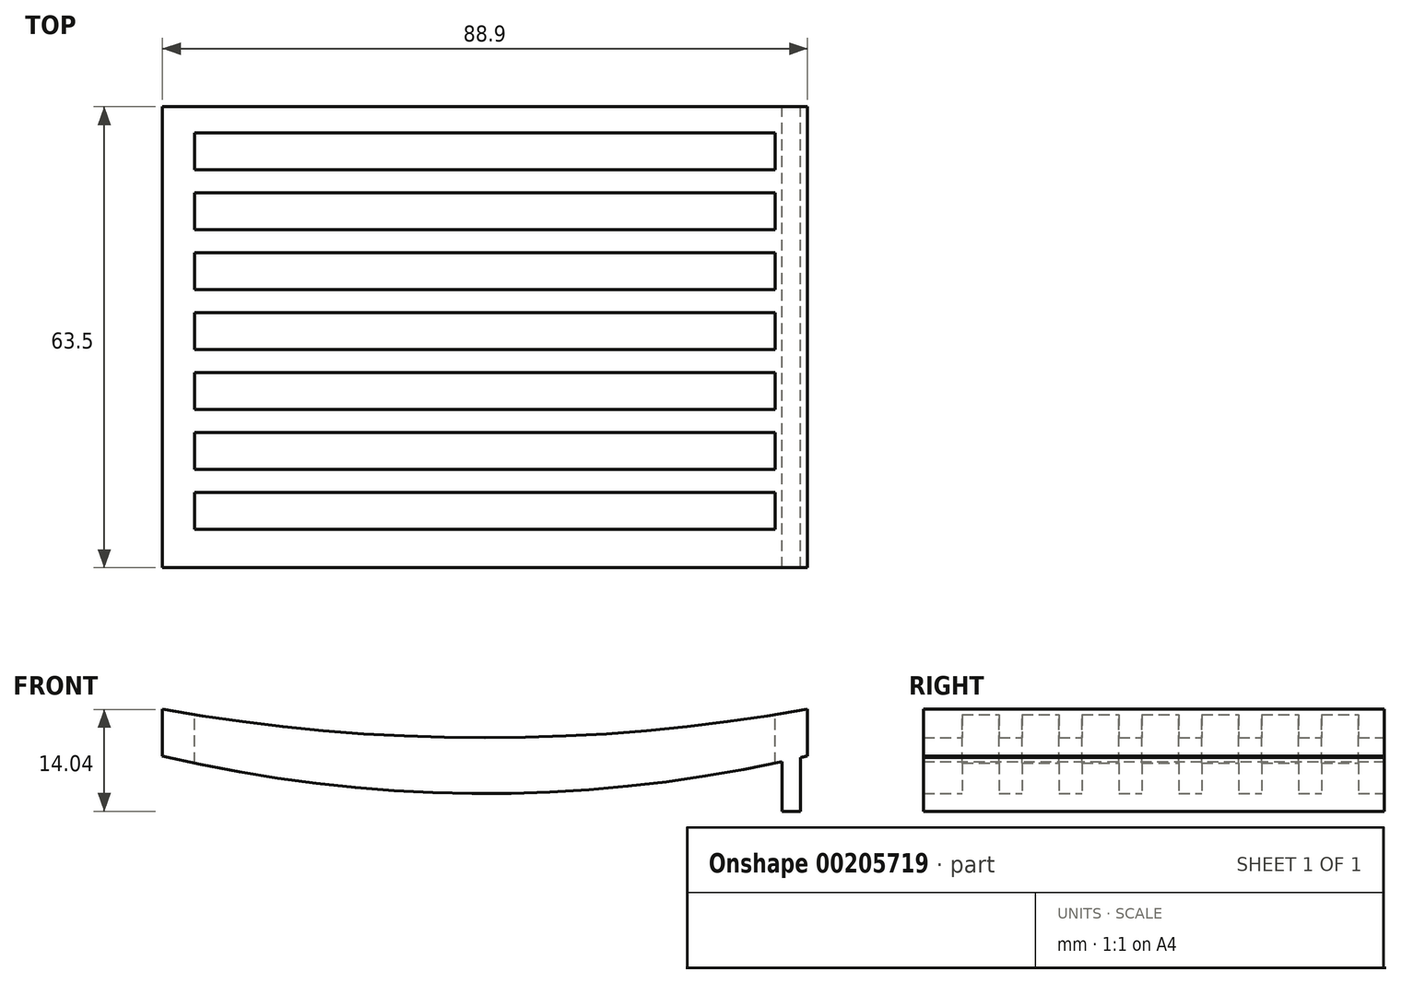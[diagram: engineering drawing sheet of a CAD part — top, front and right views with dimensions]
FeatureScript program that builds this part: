
annotation { "Feature Type Name" : "Feature", "Feature Type Description" : "" }
export const myFeature = defineFeature(function(context is Context, id is Id, definition is map)
    precondition{}
    {
        {
            var Q0;
            Q0=qCreatedBy(makeId("Front.planeOp"),FACE);
            var sketch = newSketch(context, id + "F0", { "sketchPlane" : qUnion([Q0])});
            skLineSegment(sketch, "E0.left", {"start": v(44.45, 6.42) * mm, "end": v(44.45, 0) * mm});
            skLineSegment(sketch, "E0.right", {"start": v(-44.45, 6.42) * mm, "end": v(-44.45, 0) * mm});
            skPoint(sketch, "E0.middle", {"position": v(0, 0) * mm});
            skArc(sketch, "E1", {"start": v(-44.45, 6.42) * mm, "mid": v(0, 2.5) * mm, "end": v(44.45, 6.42) * mm});
            skArc(sketch, "E2", {"start": v(-44.45, 0) * mm, "mid": v(0, -5.17) * mm, "end": v(44.45, 0) * mm});
            skSolve(sketch);
        }
        {
            var Q0;
            Q0 = qSketchRegion(id + "F0", true);
            extrude(context, id + "F1", {"entities" : qUnion([Q0]), "depth" : 63.5 * mm});
        }
        {
            var Q0;
            Q0=qCreatedBy(makeId("Top.planeOp"),FACE);
            var sketch = newSketch(context, id + "F2", { "sketchPlane" : qUnion([Q0])});
            skLineSegment(sketch, "E3.bottom", {"start": v(-40, -3.57) * mm, "end": v(40, -3.57) * mm});
            skLineSegment(sketch, "E3.top", {"start": v(-40, -8.65) * mm, "end": v(40, -8.65) * mm});
            skLineSegment(sketch, "E3.left", {"start": v(-40, -3.57) * mm, "end": v(-40, -8.65) * mm});
            skLineSegment(sketch, "E3.right", {"start": v(40, -3.57) * mm, "end": v(40, -8.65) * mm});
            skPoint(sketch, "E3.middle", {"position": v(0, -6.1) * mm});
            skLineSegment(sketch, "E4.0.1.0", {"start": v(-40, -11.82) * mm, "end": v(40, -11.82) * mm});
            skLineSegment(sketch, "E4.0.1.1", {"start": v(-40, -11.82) * mm, "end": v(-40, -16.9) * mm});
            skPoint(sketch, "E4.0.1.2", {"position": v(0, -14.36) * mm});
            skLineSegment(sketch, "E4.0.1.3", {"start": v(-40, -16.9) * mm, "end": v(40, -16.9) * mm});
            skLineSegment(sketch, "E4.0.1.4", {"start": v(40, -11.82) * mm, "end": v(40, -16.9) * mm});
            skLineSegment(sketch, "E4.0.2.0", {"start": v(-40, -20.08) * mm, "end": v(40, -20.08) * mm});
            skLineSegment(sketch, "E4.0.2.1", {"start": v(-40, -20.08) * mm, "end": v(-40, -25.16) * mm});
            skPoint(sketch, "E4.0.2.2", {"position": v(0, -22.62) * mm});
            skLineSegment(sketch, "E4.0.2.3", {"start": v(-40, -25.16) * mm, "end": v(40, -25.16) * mm});
            skLineSegment(sketch, "E4.0.2.4", {"start": v(40, -20.08) * mm, "end": v(40, -25.16) * mm});
            skLineSegment(sketch, "E4.0.3.0", {"start": v(-40, -28.33) * mm, "end": v(40, -28.33) * mm});
            skLineSegment(sketch, "E4.0.3.1", {"start": v(-40, -28.33) * mm, "end": v(-40, -33.41) * mm});
            skPoint(sketch, "E4.0.3.2", {"position": v(0, -30.87) * mm});
            skLineSegment(sketch, "E4.0.3.3", {"start": v(-40, -33.41) * mm, "end": v(40, -33.41) * mm});
            skLineSegment(sketch, "E4.0.3.4", {"start": v(40, -28.33) * mm, "end": v(40, -33.41) * mm});
            skLineSegment(sketch, "E4.0.4.0", {"start": v(-40, -36.59) * mm, "end": v(40, -36.59) * mm});
            skLineSegment(sketch, "E4.0.4.1", {"start": v(-40, -36.59) * mm, "end": v(-40, -41.67) * mm});
            skPoint(sketch, "E4.0.4.2", {"position": v(0, -39.13) * mm});
            skLineSegment(sketch, "E4.0.4.3", {"start": v(-40, -41.67) * mm, "end": v(40, -41.67) * mm});
            skLineSegment(sketch, "E4.0.4.4", {"start": v(40, -36.59) * mm, "end": v(40, -41.67) * mm});
            skLineSegment(sketch, "E4.0.5.0", {"start": v(-40, -44.84) * mm, "end": v(40, -44.84) * mm});
            skLineSegment(sketch, "E4.0.5.1", {"start": v(-40, -44.84) * mm, "end": v(-40, -49.92) * mm});
            skPoint(sketch, "E4.0.5.2", {"position": v(0, -47.38) * mm});
            skLineSegment(sketch, "E4.0.5.3", {"start": v(-40, -49.92) * mm, "end": v(40, -49.92) * mm});
            skLineSegment(sketch, "E4.0.5.4", {"start": v(40, -44.84) * mm, "end": v(40, -49.92) * mm});
            skLineSegment(sketch, "E4.0.6.0", {"start": v(-40, -53.1) * mm, "end": v(40, -53.1) * mm});
            skLineSegment(sketch, "E4.0.6.1", {"start": v(-40, -53.1) * mm, "end": v(-40, -58.18) * mm});
            skPoint(sketch, "E4.0.6.2", {"position": v(0, -55.64) * mm});
            skLineSegment(sketch, "E4.0.6.3", {"start": v(-40, -58.18) * mm, "end": v(40, -58.18) * mm});
            skLineSegment(sketch, "E4.0.6.4", {"start": v(40, -53.1) * mm, "end": v(40, -58.18) * mm});
            skLineSegment(sketch, "E4.direction1", {"start": v(-40, -8.65) * mm, "end": v(9.02, -8.65) * mm, "construction": true});
            skLineSegment(sketch, "E4.direction2", {"start": v(-40, -8.65) * mm, "end": v(-40, -16.9) * mm, "construction": true});
            skSolve(sketch);
        }
        {
            var Q0;
            Q0 = qSketchRegion(id + "F2", true);
            extrude(context, id + "F3", {"entities" : qUnion([Q0]), "operationType" : NewBodyOperationType.REMOVE, "endBound" : BoundingType.SYMMETRIC, "oppositeDirection" : true, "depth" : 50.8 * mm});
        }
        {
            var Q0;
            Q0=qCreatedBy(makeId("Top.planeOp"),FACE);
            cPlane(context, id + "F4", {"entities" : qUnion([Q0]), "cplaneType" : CPlaneType.OFFSET, "offset" : 7.62 * mm, "oppositeDirection" : true, "width" : 152.4 * mm, "height" : 152.4 * mm});
        }
        {
            var Q0;
            Q0=qCreatedBy(id+"F4.planeOp",FACE);
            var sketch = newSketch(context, id + "F5", { "sketchPlane" : qUnion([Q0])});
            skLineSegment(sketch, "E5.0.0", {"start": v(-44.45, 0) * mm, "end": v(44.45, 0) * mm});
            skLineSegment(sketch, "E5.0.1", {"start": v(44.45, 0) * mm, "end": v(44.45, -63.5) * mm});
            skLineSegment(sketch, "E5.0.2", {"start": v(44.45, -63.5) * mm, "end": v(-44.45, -63.5) * mm});
            skLineSegment(sketch, "E5.0.3", {"start": v(-44.45, -63.5) * mm, "end": v(-44.45, 0) * mm});
            skLineSegment(sketch, "E6.0", {"start": v(-40, -58.18) * mm, "end": v(40, -58.18) * mm});
            skPoint(sketch, "E7.0", {"position": v(-40, -55.64) * mm});
            skLineSegment(sketch, "E8.0", {"start": v(-40, -53.1) * mm, "end": v(-40, -58.18) * mm});
            skLineSegment(sketch, "E9.0", {"start": v(-40, -53.1) * mm, "end": v(40, -53.1) * mm});
            skLineSegment(sketch, "E10", {"start": v(-40, -58.18) * mm, "end": v(-44.45, -58.18) * mm});
            skLineSegment(sketch, "E11.bottom", {"start": v(-40.96, -63.5) * mm, "end": v(-43.5, -63.5) * mm});
            skLineSegment(sketch, "E11.top", {"start": v(-40.96, 0) * mm, "end": v(-43.5, 0) * mm});
            skLineSegment(sketch, "E11.left", {"start": v(-40.96, -63.5) * mm, "end": v(-40.96, 0) * mm});
            skLineSegment(sketch, "E11.right", {"start": v(-43.5, -63.5) * mm, "end": v(-43.5, 0) * mm});
            skPoint(sketch, "E11.middle", {"position": v(-42.23, -31.75) * mm});
            skPoint(sketch, "E11.middle.positionSnap0", {"position": v(-44.45, -31.75) * mm});
            skPoint(sketch, "E11.middle.positionSnap1", {"position": v(-42.23, -58.18) * mm});
            skPoint(sketch, "E11.centerSnap0", {"position": v(-44.45, -31.75) * mm});
            skPoint(sketch, "E11.centerSnap1", {"position": v(-42.23, -58.18) * mm});
            skLineSegment(sketch, "E12", {"start": v(0, -63.5) * mm, "end": v(0, -71.29) * mm});
            skLineSegment(sketch, "E13.MirrorCS", {"start": v(40.96, -63.5) * mm, "end": v(40.96, 0) * mm});
            skLineSegment(sketch, "E14.MirrorCS", {"start": v(43.5, -63.5) * mm, "end": v(43.5, 0) * mm});
            skLineSegment(sketch, "E15.MirrorCS", {"start": v(40.96, -63.5) * mm, "end": v(43.5, -63.5) * mm});
            skLineSegment(sketch, "E16.MirrorCS", {"start": v(40.96, 0) * mm, "end": v(43.5, 0) * mm});
            skSolve(sketch);
        }
        {
            var Q0;
            {var subQ5=sQuery(id+"F5.wireOp",EDGE,"E11.top");Q0=makeQuery(id+"F5.imprint","IMPRINT",FACE,{"disambiguationData":[TD([[makeQuery(id+"F5.imprint","IMPRINT",EDGE,{"derivedFrom":subQ5}),1.0]])]});}
            var Q1;
            {var subQ5=sQuery(id+"F5.wireOp",EDGE,"E11.bottom");Q1=makeQuery(id+"F5.imprint","IMPRINT",FACE,{"disambiguationData":[TD([[makeQuery(id+"F5.imprint","IMPRINT",EDGE,{"derivedFrom":subQ5}),-1.0]])]});}
            var Q2;
            Q2=makeQuery(id+"F5.imprint","IMPRINT",FACE,{"disambiguationData":[TD([[makeQuery(id+"F5.imprint","IMPRINT",EDGE,{"derivedFrom":sQuery(id+"F5.wireOp",EDGE,"E13.MirrorCS")}),-1.0]])]});
            extrude(context, id + "F6", {"entities" : qUnion([Q0, Q1, Q2]), "operationType" : NewBodyOperationType.ADD, "endBound" : BoundingType.UP_TO_NEXT, "depth" : 25.4 * mm});
        }
    });
